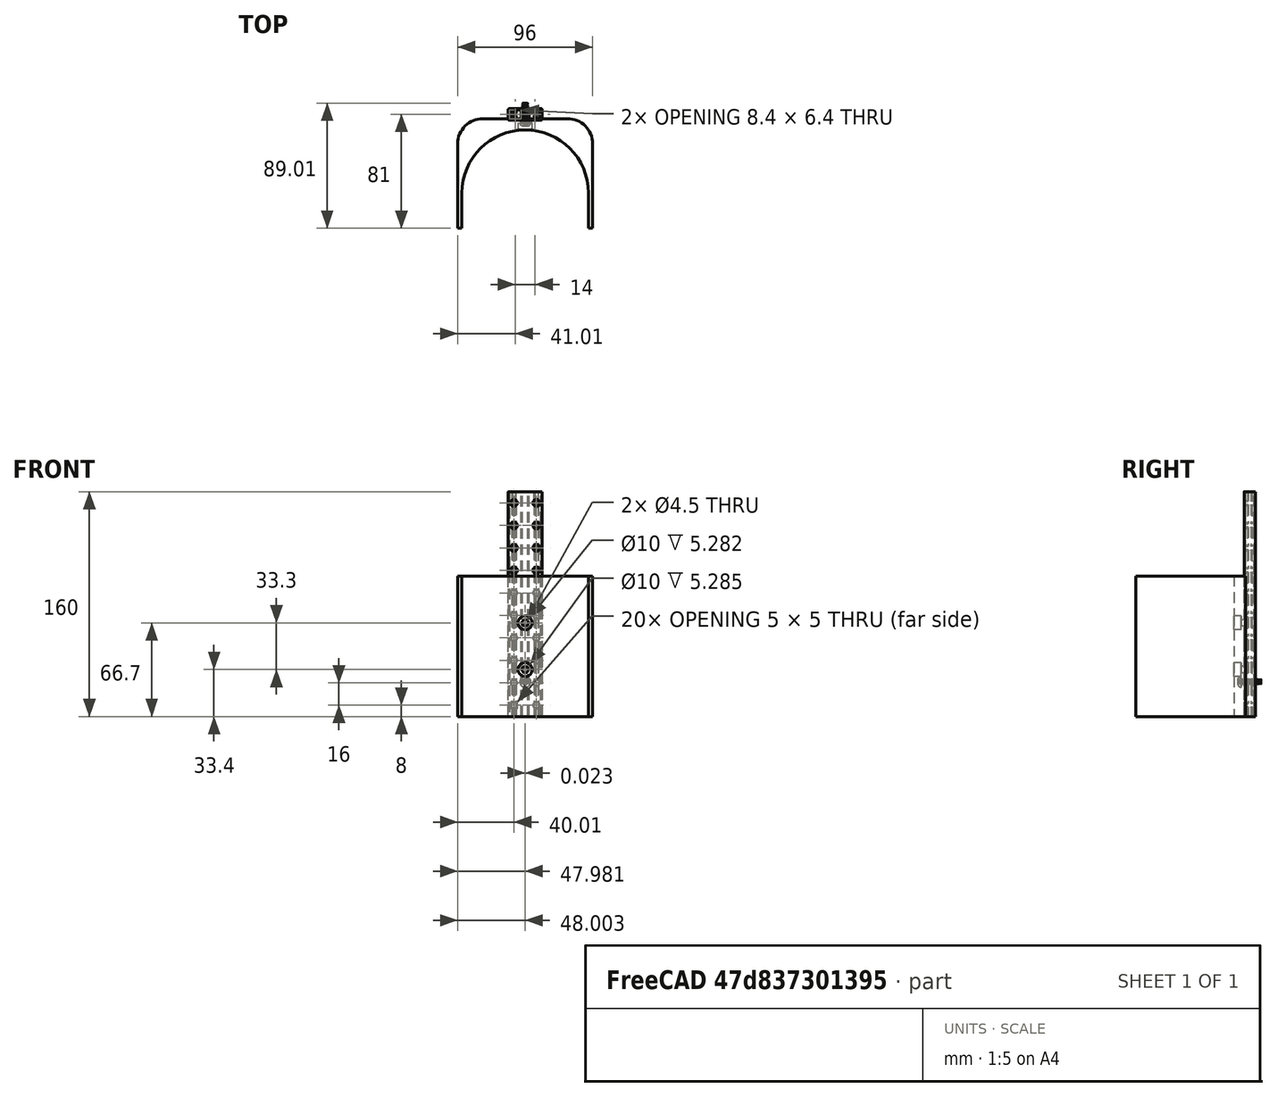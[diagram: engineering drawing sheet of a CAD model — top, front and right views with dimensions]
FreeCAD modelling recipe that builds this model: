
FCSTD DOCUMENT  (FreeCAD 0.21R33675 (Git))
Label: Mx 20223 Feeder Support
License: All rights reserved
LicenseURL: http://en.wikipedia.org/wiki/All_rights_reserved
objects: Sketcher::SketchObject×3, PartDesign::Pocket×2, Part::Feature×2, PartDesign::Pad×1, Mesh::Feature×1, PartDesign::Plane×1, PartDesign::Body×1
note: 13 computed .brp shape members not serialized (recipe doc carries the construction recipe); baked Part::Feature solids carry a one-line shape summary decoded from their .brp

FEATURE [Sketcher::SketchObject] Sketch
  FullyConstrained = false
  MapMode = 5
  Support = -> [XY_Plane]
  sketch-geometry (10):
    g0: LineSegment StartX=17.9935 StartY=77.9965 StartZ=0 EndX=77.9935 EndY=77.9965 EndZ=0
    g1: LineSegment StartX=-0.006468 StartY=59.9965 StartZ=0 EndX=-0.006468 EndY=-0.003482 EndZ=0
    g2: LineSegment StartX=95.9935 StartY=59.9965 StartZ=0 EndX=95.9935 EndY=-0.003482 EndZ=0
    g3: ArcOfCircle CenterX=47.9935 CenterY=24.9965 CenterZ=0 NormalX=0 NormalY=0 NormalZ=1 AngleXU=0 Radius=45 StartAngle=1e-16 EndAngle=3.14159
    g4: LineSegment StartX=-0.006468 StartY=-0.003482 StartZ=0 EndX=2.99353 EndY=-0.003482 EndZ=0
    g5: LineSegment StartX=95.9935 StartY=-0.003482 StartZ=0 EndX=92.9935 EndY=-0.003482 EndZ=0
    g6: LineSegment StartX=92.9935 StartY=24.9965 StartZ=0 EndX=92.9935 EndY=-0.003482 EndZ=0
    g7: LineSegment StartX=2.99353 StartY=-0.003482 StartZ=0 EndX=2.99353 EndY=24.9965 EndZ=0
    g8: ArcOfCircle CenterX=17.9935 CenterY=59.9965 CenterZ=0 NormalX=0 NormalY=0 NormalZ=1 AngleXU=0 Radius=18 StartAngle=1.5708 EndAngle=3.14159
    g9: ArcOfCircle CenterX=77.9935 CenterY=59.9965 CenterZ=0 NormalX=0 NormalY=0 NormalZ=1 AngleXU=0 Radius=18 StartAngle=0 EndAngle=1.5708
  constraints (27):
    c: Horizontal(g0)
    c: Vertical(g1)
    c: Vertical(g2)
    c: Equal(g1,g2)
    c: Angle(g3) = 3.14159
    c: Coincident(g4,g1)
    c: Horizontal(g4)
    c: Coincident(g5,g2)
    c: Equal(g4,g5)
    c: DistanceX(g4,g4) = 3
    c: Angle(g5,g2,g2) = 1.5708
    c: Coincident(g6,g3)
    c: Coincident(g6,g5)
    c: Coincident(g7,g4)
    c: Coincident(g7,g3)
    c: Vertical(g7)
    c: Diameter(g3) = 90
    c: DistanceY(g7,g7) = 25
    c: Equal(g7,g6)
    c: Tangent(g0,g8) = 1.5708
    c: Tangent(g1,g8) = -1.5708
    c: Tangent(g0,g9) = 1.5708
    c: Tangent(g2,g9) = 1.5708
    c: DistanceX(g0,g0) = 60
    c: DistanceY(g1,g1) = 60
    c: Equal(g8,g9)
    c: Angle(g5,g6) = 1.5708
FEATURE [PartDesign::Pad] Pad
  Direction = (0,0,1)
  Length = 100
  Length2 = 10
  Profile = -> Sketch
  ReferenceAxis = -> Sketch [N_Axis]
  Type = 0
FEATURE [Mesh::Feature] Fantastic_Jaagub  label="Fantastic Jaagub"
  Placement = pos=(39,63,0) rot=(0,0,1;0rad)
FEATURE [PartDesign::Plane] DatumPlane
  AttachmentOffset = pos=(0,0,-65) rot=(0,0,1;0rad)
  Length = 145.59
  MapMode = 3
  Placement = pos=(0,65,-1.44e-14) rot=(1,0,0;1.5708rad)
  ResizeMode = 0
  Support = -> [Pad]
  Width = 149.596
FEATURE [Sketcher::SketchObject] Sketch001
  ExternalGeometry = -> [Pad]
  FullyConstrained = false
  MapMode = 5
  Placement = pos=(0,65,-1.44e-14) rot=(1,0,0;1.5708rad)
  Support = -> [DatumPlane]
  sketch-geometry (2):
    g0: Circle CenterX=47.9935 CenterY=66.7 CenterZ=0 NormalX=0 NormalY=0 NormalZ=1 AngleXU=0 Radius=5
    g1: Circle CenterX=47.9708 CenterY=33.4 CenterZ=0 NormalX=0 NormalY=0 NormalZ=1 AngleXU=0 Radius=5
  constraints (5):
    c: Diameter(g0) = 10
    c: DistanceX(g0,g-6) = 45
    c: DistanceY(g0,g-5) = 33.3
    c: Diameter(g1) = 10
    c: DistanceY(g1,g0) = 33.3
FEATURE [PartDesign::Pocket] Pocket
  BaseFeature = -> Pad
  Direction = (0,1,-2e-16)
  Length = 10
  Length2 = 5
  Profile = -> Sketch001
  ReferenceAxis = -> Sketch001 [N_Axis]
  Type = 0
FEATURE [Sketcher::SketchObject] Sketch002
  ExternalGeometry = -> [Pocket]
  FullyConstrained = true
  MapMode = 5
  Placement = pos=(-3.52e-14,75,-1.27e-14) rot=(1,0,0;1.5708rad)
  Support = -> [Pocket]
  sketch-geometry (2):
    g0: Circle CenterX=47.9935 CenterY=66.7 CenterZ=0 NormalX=0 NormalY=0 NormalZ=1 AngleXU=0 Radius=2.25
    g1: Circle CenterX=47.9709 CenterY=33.4 CenterZ=0 NormalX=0 NormalY=0 NormalZ=1 AngleXU=0 Radius=2.25
  constraints (4):
    c: Coincident(g0,g-3)
    c: Diameter(g0) = 4.5
    c: Coincident(g1,g-4)
    c: Diameter(g1) = 4.5
FEATURE [PartDesign::Pocket] Pocket001
  BaseFeature = -> Pocket
  Direction = (-5e-16,1,-2e-16)
  Length = 5
  Length2 = 5
  Profile = -> Sketch002
  ReferenceAxis = -> Sketch002 [N_Axis]
  Type = 0
FEATURE [PartDesign::Body] Body  label="Feeder-Full-Height"
  Group = -> [Sketch,Pad,DatumPlane,Sketch001,Pocket,Sketch002,Pocket001]
  Origin = -> Origin
  Tip = -> Pocket001
FEATURE [Part::Feature] Part__Feature  label="Hexagon socket button head screws M4"
  Placement = pos=(48,89,24.8) rot=(0.01,0,0.99995;1.5708rad)
  shape: bbox 8.227 x 16.25 x 15.28 mm, 101 faces (baked)
FEATURE [Part::Feature] Part__Feature001  label="Beam0824-160˫¿؁º"
  Placement = pos=(48,77,0) rot=(0,0,1;0rad)
  shape: bbox 24 x 8 x 160 mm, 726 faces (baked)
